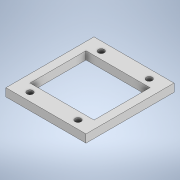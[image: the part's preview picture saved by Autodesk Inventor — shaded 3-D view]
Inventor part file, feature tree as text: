
AUTODESK INVENTOR PART (.ipt)
format: ipt  version: 2022 (Build 260153000, 153)  size: 117,248 bytes
history: native  units: mm
features: extrude x1, sketch x1
ambient origin geometry x8: Origin, YZ Plane, XZ Plane, XY Plane, X Axis, Y Axis, Z Axis, Center Point
bodies: Solid1 (feature_tree)
feature tree (2):
  extrude  "Extrusion1"  Depth=11.0mm
  sketch  "Sketch1"  dims[d0=10.0mm d1=11.0mm d2=5.5mm d3=7.5mm d4=8.0mm d5=7.0mm d6=2.0mm d7=1.0mm d8=0.75mm d9=2.0mm d10=1.0mm d11=20.0mm d13=8.9mm d14=20.0mm d16=6.0mm d19=1.0mm d20=0.0mm]
